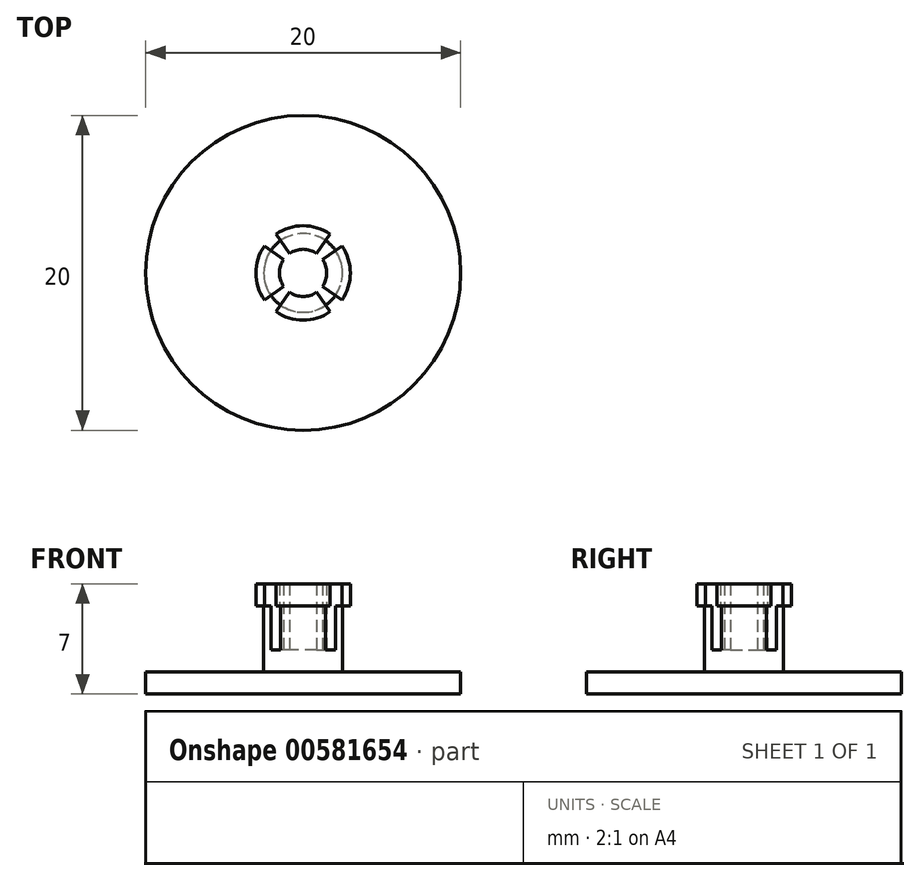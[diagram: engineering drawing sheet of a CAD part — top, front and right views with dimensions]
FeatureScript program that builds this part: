
annotation { "Feature Type Name" : "Feature", "Feature Type Description" : "" }
export const myFeature = defineFeature(function(context is Context, id is Id, definition is map)
    precondition{}
    {
        {
            var Q0;
            Q0=qCreatedBy(makeId("Top.planeOp"),FACE);
            var sketch = newSketch(context, id + "F0", { "sketchPlane" : qUnion([Q0])});
            skCircle(sketch, "E0", {"center": v(0, 0) * mm, "radius": 10 * mm});
            skSolve(sketch);
        }
        {
            var Q0;
            Q0 = qSketchRegion(id + "F0", true);
            extrude(context, id + "F1", {"entities" : qUnion([Q0]), "depth" : 1.4 * mm, "offsetDistance" : 25 * mm});
        }
        {
            var Q0;
            Q0=makeQuery(id+"F1.opExtrude","CAP_FACE",FACE,{"disambiguationData":[OSD([sQuery(id+"F0.wireOp",EDGE,"E0")])],"isStart":false});
            var sketch = newSketch(context, id + "F2", { "sketchPlane" : qUnion([Q0])});
            skCircle(sketch, "E1", {"center": v(0, 0) * mm, "radius": 2.5 * mm});
            skSolve(sketch);
        }
        {
            var Q0;
            Q0 = qSketchRegion(id + "F2", true);
            extrude(context, id + "F3", {"entities" : qUnion([Q0]), "operationType" : NewBodyOperationType.ADD, "depth" : 1.4 * mm, "offsetDistance" : 25 * mm});
        }
        {
            var Q0;
            Q0=makeQuery(id+"F3.opExtrude","CAP_FACE",FACE,{"disambiguationData":[OSD([sQuery(id+"F2.wireOp",EDGE,"E1")])],"isStart":false});
            var sketch = newSketch(context, id + "F4", { "sketchPlane" : qUnion([Q0])});
            skCircle(sketch, "E2", {"center": v(0, 0) * mm, "radius": 1.5 * mm});
            skCircle(sketch, "E3", {"center": v(0, 0) * mm, "radius": 2.5 * mm});
            skLineSegment(sketch, "E4", {"start": v(0, 0) * mm, "end": v(1.43, 2.05) * mm});
            skLineSegment(sketch, "E5", {"start": v(0, 0) * mm, "end": v(2.05, 1.43) * mm});
            skLineSegment(sketch, "E6", {"start": v(0, 0) * mm, "end": v(2.05, -1.43) * mm});
            skLineSegment(sketch, "E7", {"start": v(0, 0) * mm, "end": v(1.43, -2.05) * mm});
            skLineSegment(sketch, "E8", {"start": v(0, 0) * mm, "end": v(-1.43, -2.05) * mm});
            skLineSegment(sketch, "E9", {"start": v(0, 0) * mm, "end": v(-2.05, -1.43) * mm});
            skLineSegment(sketch, "E10", {"start": v(0, 0) * mm, "end": v(-2.05, 1.43) * mm});
            skLineSegment(sketch, "E11", {"start": v(0, 0) * mm, "end": v(-1.43, 2.05) * mm});
            skPoint(sketch, "E12", {"position": v(-1.23, 0.86) * mm});
            skPoint(sketch, "E13", {"position": v(-0.86, 1.23) * mm});
            skPoint(sketch, "E14", {"position": v(0.86, 1.23) * mm});
            skPoint(sketch, "E15", {"position": v(1.23, 0.86) * mm});
            skPoint(sketch, "E16", {"position": v(1.23, -0.86) * mm});
            skPoint(sketch, "E17", {"position": v(-0.86, -1.23) * mm});
            skPoint(sketch, "E18", {"position": v(0.86, -1.23) * mm});
            skPoint(sketch, "E19", {"position": v(-1.23, -0.86) * mm});
            skSolve(sketch);
        }
        {
            var Q0;
            {var subQ0=sQuery(id+"F4.wireOp",EDGE,"E10");var subQ1=sQuery(id+"F4.wireOp",EDGE,"E2");var subQ2=makeQuery(id+"F4.imprint","INTERSECT",VERTEX,{"derivedFrom":[subQ1,subQ0]});Q0=makeQuery(id+"F4.imprint","IMPRINT",FACE,{"disambiguationData":[TD([[makeQuery(id+"F4.imprint","IMPRINT",EDGE,{"disambiguationData":[TD([[subQ2,-1.0]])],"derivedFrom":subQ1}),-1.0]])]});}
            var Q1;
            {var subQ4=sQuery(id+"F4.wireOp",EDGE,"E2");var subQ6=sQuery(id+"F4.wireOp",EDGE,"E4");var subQ8=makeQuery(id+"F4.imprint","INTERSECT",VERTEX,{"derivedFrom":[subQ4,subQ6]});Q1=makeQuery(id+"F4.imprint","IMPRINT",FACE,{"disambiguationData":[TD([[makeQuery(id+"F4.imprint","IMPRINT",EDGE,{"disambiguationData":[TD([[subQ8,-1.0]])],"derivedFrom":subQ4}),-1.0]])]});}
            var Q2;
            {var subQ0=sQuery(id+"F4.wireOp",EDGE,"E5");var subQ1=sQuery(id+"F4.wireOp",EDGE,"E2");var subQ2=makeQuery(id+"F4.imprint","INTERSECT",VERTEX,{"derivedFrom":[subQ1,subQ0]});Q2=makeQuery(id+"F4.imprint","IMPRINT",FACE,{"disambiguationData":[TD([[makeQuery(id+"F4.imprint","IMPRINT",EDGE,{"disambiguationData":[TD([[subQ2,1.0]])],"derivedFrom":subQ1}),-1.0]])]});}
            var Q3;
            {var subQ0=sQuery(id+"F4.wireOp",EDGE,"E8");var subQ1=sQuery(id+"F4.wireOp",EDGE,"E2");var subQ2=makeQuery(id+"F4.imprint","INTERSECT",VERTEX,{"derivedFrom":[subQ1,subQ0]});Q3=makeQuery(id+"F4.imprint","IMPRINT",FACE,{"disambiguationData":[TD([[makeQuery(id+"F4.imprint","IMPRINT",EDGE,{"disambiguationData":[TD([[subQ2,-1.0]])],"derivedFrom":subQ1}),-1.0]])]});}
            extrude(context, id + "F5", {"entities" : qUnion([Q0, Q1, Q2, Q3]), "operationType" : NewBodyOperationType.ADD, "depth" : 2.8 * mm, "offsetDistance" : 25 * mm});
        }
        {
            var Q0;
            Q0=makeQuery(id+"F5.opExtrude","CAP_FACE",FACE,{"disambiguationData":[OSD([sQuery(id+"F4.wireOp",EDGE,"E2"),sQuery(id+"F4.wireOp",EDGE,"E3"),sQuery(id+"F4.wireOp",EDGE,"E4"),sQuery(id+"F4.wireOp",EDGE,"E11"),sQuery(id+"F4.wireOp",EDGE,"NBkQQOMy-s0Cz-SMjw-Mwqk-ynoo35NlcCDb")])],"isStart":false});
            var sketch = newSketch(context, id + "F6", { "sketchPlane" : qUnion([Q0])});
            skArc(sketch, "E20.0", {"start": v(0.86, 1.23) * mm, "mid": v(0, 1.5) * mm, "end": v(-0.86, 1.23) * mm});
            skLineSegment(sketch, "E20.1", {"start": v(-0.86, 1.23) * mm, "end": v(-1.43, 2.05) * mm});
            skLineSegment(sketch, "E20.2", {"start": v(0.86, 1.23) * mm, "end": v(1.43, 2.05) * mm});
            skLineSegment(sketch, "E20.3", {"start": v(1.23, 0.86) * mm, "end": v(2.05, 1.43) * mm});
            skArc(sketch, "E20.4", {"start": v(1.23, -0.86) * mm, "mid": v(1.5, 0) * mm, "end": v(1.23, 0.86) * mm});
            skLineSegment(sketch, "E20.5", {"start": v(1.23, -0.86) * mm, "end": v(2.05, -1.43) * mm});
            skLineSegment(sketch, "E20.6", {"start": v(0.86, -1.23) * mm, "end": v(1.43, -2.05) * mm});
            skArc(sketch, "E20.7", {"start": v(-0.86, -1.23) * mm, "mid": v(0, -1.5) * mm, "end": v(0.86, -1.23) * mm});
            skLineSegment(sketch, "E20.8", {"start": v(-0.86, -1.23) * mm, "end": v(-1.43, -2.05) * mm});
            skLineSegment(sketch, "E20.9", {"start": v(-1.23, -0.86) * mm, "end": v(-2.05, -1.43) * mm});
            skArc(sketch, "E20.10", {"start": v(-1.23, 0.86) * mm, "mid": v(-1.5, 0) * mm, "end": v(-1.23, -0.86) * mm});
            skLineSegment(sketch, "E20.11", {"start": v(-1.23, 0.86) * mm, "end": v(-2.05, 1.43) * mm});
            skCircle(sketch, "E21", {"center": v(0, 0) * mm, "radius": 3 * mm});
            skLineSegment(sketch, "E22", {"start": v(-1.23, 0.86) * mm, "end": v(-2.46, 1.72) * mm});
            skLineSegment(sketch, "E23", {"start": v(-1.23, -0.86) * mm, "end": v(-2.46, -1.72) * mm});
            skLineSegment(sketch, "E24", {"start": v(-0.86, -1.23) * mm, "end": v(-1.72, -2.46) * mm});
            skLineSegment(sketch, "E25", {"start": v(0.86, -1.23) * mm, "end": v(1.72, -2.46) * mm});
            skLineSegment(sketch, "E26", {"start": v(1.23, -0.86) * mm, "end": v(2.46, -1.72) * mm});
            skLineSegment(sketch, "E27", {"start": v(1.23, 0.86) * mm, "end": v(2.46, 1.72) * mm});
            skLineSegment(sketch, "E28", {"start": v(0.86, 1.23) * mm, "end": v(1.72, 2.46) * mm});
            skLineSegment(sketch, "E29", {"start": v(-0.86, 1.23) * mm, "end": v(-1.72, 2.46) * mm});
            skPoint(sketch, "E30", {"position": v(-2.46, 1.72) * mm});
            skPoint(sketch, "E31", {"position": v(-2.46, -1.72) * mm});
            skPoint(sketch, "E32", {"position": v(-1.72, -2.46) * mm});
            skPoint(sketch, "E33", {"position": v(1.72, -2.46) * mm});
            skPoint(sketch, "E34", {"position": v(2.46, -1.72) * mm});
            skPoint(sketch, "E35", {"position": v(2.46, 1.72) * mm});
            skPoint(sketch, "E36", {"position": v(1.72, 2.46) * mm});
            skPoint(sketch, "E37", {"position": v(-1.72, 2.46) * mm});
            skSolve(sketch);
        }
        {
            var Q0;
            {var subQ1=sQuery(id+"F6.wireOp",EDGE,"E20.10");Q0=makeQuery(id+"F6.imprint","IMPRINT",FACE,{"disambiguationData":[TD([[makeQuery(id+"F6.imprint","IMPRINT",EDGE,{"derivedFrom":subQ1}),-1.0]])]});}
            var Q1;
            {var subQ1=sQuery(id+"F6.wireOp",EDGE,"E20.7");Q1=makeQuery(id+"F6.imprint","IMPRINT",FACE,{"disambiguationData":[TD([[makeQuery(id+"F6.imprint","IMPRINT",EDGE,{"derivedFrom":subQ1}),-1.0]])]});}
            var Q2;
            {var subQ1=sQuery(id+"F6.wireOp",EDGE,"E20.4");Q2=makeQuery(id+"F6.imprint","IMPRINT",FACE,{"disambiguationData":[TD([[makeQuery(id+"F6.imprint","IMPRINT",EDGE,{"derivedFrom":subQ1}),-1.0]])]});}
            var Q3;
            {var subQ0=sQuery(id+"F6.wireOp",EDGE,"E20.0");Q3=makeQuery(id+"F6.imprint","IMPRINT",FACE,{"disambiguationData":[TD([[makeQuery(id+"F6.imprint","IMPRINT",EDGE,{"derivedFrom":subQ0}),-1.0]])]});}
            var Q4;
            {var subQ5=sQuery(id+"F4.wireOp",EDGE,"E3");var subQ6=makeQuery(id+"F5.opExtrude","CAP_EDGE",EDGE,{"disambiguationData":[OSD([subQ5]),TDD([makeQuery(id+"F4.imprint","IMPRINT",EDGE,{"disambiguationData":[TD([[makeQuery(id+"F4.imprint","INTERSECT",VERTEX,{"derivedFrom":[subQ5,sQuery(id+"F4.wireOp",EDGE,"E4")]}),-1.0]])],"derivedFrom":subQ5})])],"isStart":false});Q4=makeQuery(id+"F6.imprint","IMPRINT",FACE,{"disambiguationData":[TD([[makeQuery(id+"F6.imprint","IMPRINT",EDGE,{"derivedFrom":subQ6}),-1.0]])]});}
            extrude(context, id + "F7", {"entities" : qUnion([Q0, Q1, Q2, Q3, Q4]), "operationType" : NewBodyOperationType.ADD, "depth" : 1.4 * mm, "offsetDistance" : 25 * mm});
        }
    });
